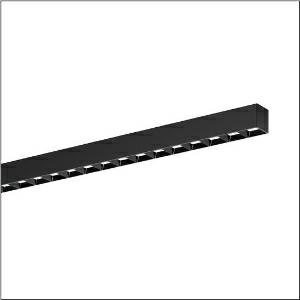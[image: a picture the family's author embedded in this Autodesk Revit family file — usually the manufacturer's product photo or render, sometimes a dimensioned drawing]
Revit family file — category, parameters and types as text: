
# Revit family: silica_r__21_51mx22dn39bb_3244
name_source: partatom
category: Lighting Fixtures
units: mm (PartAtom-declared; Revit-internal decimal feet)

## family parameters
Cut with Voids When Loaded = No
Host = Face
Light Source = No
Part Type = Normal
Room Calculation Point = No
Round Connector Dimension = Use Diameter
Shared = No

## types (1)
- --- (1 x LED, 9720 lm, 62.7 W, 3000K)
    Apparent Load = 63 VA
    CIE Flux Codes = 86 100 100 100 100
    Color Rendering = 80
    Color Temperature = 3000K
    Default Elevation = 1800 mm
    Description = Silica® 21, office luminaire, primary light control with darklight reflector, of PMMA, black, CAT 2 (L<= 3000cd/m²), light emission: direct distribution, primary light characteristic: symmetric, installation type: surface-mounted, LED, rated luminous flux: 9.720lm, luminous efficacy: 155lm/W, light colour: 830, colour temperature: 3000K, control gear: DALI 2, with terminal, 3+2-pole, max. 2.5mm², mains connection: 220..240V, AC, 50/60Hz, rated input power: 62.7W, luminaire housing, of aluminium, matt jet black (RAL 9005), length: 2.700mm, width: 53mm, height: 53mm, protection rating (complete): IP20, insulation class (complete): insulation class I (protective earthing), certification: CE, permissible operating ambient temperature: 0..+35°C, standard: EN 50419, packaging unit: 1 piece
    Height = 53 mm
    Lamp = 1 x LED
    Lamp Light Flux = 9720 lm
    Lamp Power = 62.7 W
    Lamp count = 1
    Length = 2704 mm
    Luminous efficacy = 155 lm/W
    Manufacturer = Siteco
    ModVariant = No
    Model = 51MX22DN39BB
    Mounting Place = Ceiling
    Mounting Type = Surface mounted
    Number of Poles = 1
    OnlyDefault = Yes
    Power Factor = 1
    Product Name = Silica® 21
    Product group = office luminaire | ceiling mounted
    ProductGroupID = 303
    Protection Class = Protection class I
    Protection Degree = IP 20
    RLX_Detail_Level = 1
    RLX_Emergency_Light_Flux = 0 lm
    RLX_Emergency_Type = 0
    RLX_Emergency_Type_DB = No
    RlxData = <blob elided: 36061 chars, md5=9601f4dd>
    Socket = socket
    Standby Power = 0 W
    System Light Flux = 9720 lm
    System Power = 63 W
    Type Comments = factory setting: luminous flux: 100 % | dim-lin: 254 | 392 mA
    Type Image = l_1335908.jpg
    URL = http://relux.com
    VarID = @adj_084407
    Voltage = 0 V
    Weight = 0.00 kg
    Width = 53 mm

## geometry (parser evidence)
native form markers: Blend x4, Sweep x12
no freeform markers — native parametric forms only
